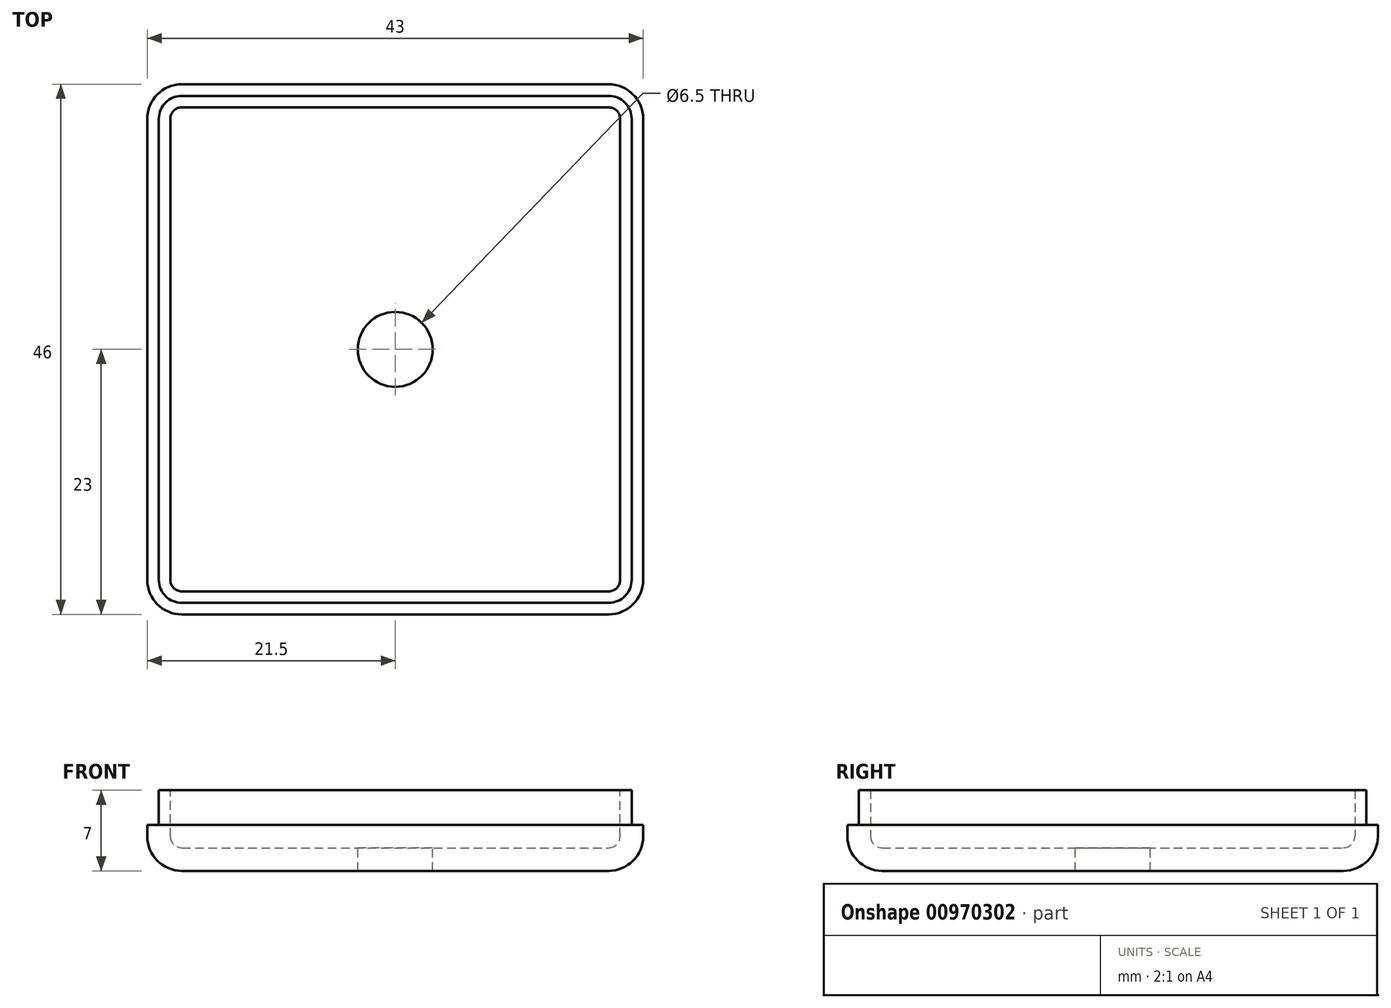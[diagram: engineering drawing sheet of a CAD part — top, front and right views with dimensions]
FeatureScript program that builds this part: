
annotation { "Feature Type Name" : "Feature", "Feature Type Description" : "" }
export const myFeature = defineFeature(function(context is Context, id is Id, definition is map)
    precondition{}
    {
        {
            var Q0;
            Q0=qCreatedBy(makeId("Top.planeOp"),FACE);
            var sketch = newSketch(context, id + "F0", { "sketchPlane" : qUnion([Q0])});
            skLineSegment(sketch, "E0.bottom", {"start": v(21.5, -23) * mm, "end": v(-21.5, -23) * mm});
            skLineSegment(sketch, "E0.top", {"start": v(21.5, 23) * mm, "end": v(-21.5, 23) * mm});
            skLineSegment(sketch, "E0.left", {"start": v(21.5, -23) * mm, "end": v(21.5, 23) * mm});
            skLineSegment(sketch, "E0.right", {"start": v(-21.5, -23) * mm, "end": v(-21.5, 23) * mm});
            skPoint(sketch, "E0.middle", {"position": v(0, 0) * mm});
            skSolve(sketch);
        }
        {
            var Q0;
            Q0=makeQuery(id+"F0.imprint","IMPRINT",FACE,{"disambiguationData":[TD([[makeQuery(id+"F0.imprint","IMPRINT",EDGE,{"derivedFrom":sQuery(id+"F0.wireOp",EDGE,"E0.bottom")}),-1.0]])]});
            extrude(context, id + "F1", {"entities" : qUnion([Q0]), "depth" : 7 * mm, "offsetDistance" : 25 * mm});
        }
        {
            var Q0;
            Q0=makeQuery(id+"F1.opExtrude","CAP_FACE",FACE,{"disambiguationData":[OSD([sQuery(id+"F0.wireOp",EDGE,"E0.bottom"),sQuery(id+"F0.wireOp",EDGE,"E0.top"),sQuery(id+"F0.wireOp",EDGE,"E0.left"),sQuery(id+"F0.wireOp",EDGE,"E0.right")])],"isStart":true});
            var Q1;
            Q1=makeQuery(id+"F1.opExtrude","SWEPT_EDGE",EDGE,{"disambiguationData":[OSD([sQuery(id+"F0.wireOp",EDGE,"E0.top"),sQuery(id+"F0.wireOp",EDGE,"E0.left")])]});
            var Q2;
            Q2=makeQuery(id+"F1.opExtrude","SWEPT_EDGE",EDGE,{"disambiguationData":[OSD([sQuery(id+"F0.wireOp",EDGE,"E0.bottom"),sQuery(id+"F0.wireOp",EDGE,"E0.left")])]});
            var Q3;
            Q3=makeQuery(id+"F1.opExtrude","SWEPT_EDGE",EDGE,{"disambiguationData":[OSD([sQuery(id+"F0.wireOp",EDGE,"E0.top"),sQuery(id+"F0.wireOp",EDGE,"E0.right")])]});
            var Q4;
            Q4=makeQuery(id+"F1.opExtrude","SWEPT_EDGE",EDGE,{"disambiguationData":[OSD([sQuery(id+"F0.wireOp",EDGE,"E0.bottom"),sQuery(id+"F0.wireOp",EDGE,"E0.right")])]});
            fillet(context, id + "F2", {"entities" : qUnion([Q0, Q1, Q2, Q3, Q4]), "radius" : 3 * mm, "tangentPropagation" : true, "allowEdgeOverflow" : false});
        }
        {
            var Q0;
            Q0=makeQuery(id+"F1.opExtrude","CAP_FACE",FACE,{"disambiguationData":[OSD([sQuery(id+"F0.wireOp",EDGE,"E0.bottom"),sQuery(id+"F0.wireOp",EDGE,"E0.top"),sQuery(id+"F0.wireOp",EDGE,"E0.left"),sQuery(id+"F0.wireOp",EDGE,"E0.right")])],"isStart":false});
            shell(context, id + "F3", {"entities" : qUnion([Q0]), "thickness" : 2 * mm});
        }
        {
            var Q0;
            Q0=makeQuery(id+"F3.opShell","OFFSET_FACE",FACE,{"disambiguationData":[OSD([sQuery(id+"F0.wireOp",EDGE,"E0.bottom"),sQuery(id+"F0.wireOp",EDGE,"E0.top"),sQuery(id+"F0.wireOp",EDGE,"E0.left"),sQuery(id+"F0.wireOp",EDGE,"E0.right")])]});
            var sketch = newSketch(context, id + "F4", { "sketchPlane" : qUnion([Q0])});
            skCircle(sketch, "E1", {"center": v(0, 0) * mm, "radius": 3.25 * mm});
            skSolve(sketch);
        }
        {
            var Q0;
            Q0=qSketchRegion(id+"F4",true);
            extrude(context, id + "F5", {"entities" : qUnion([Q0]), "operationType" : NewBodyOperationType.REMOVE, "endBound" : BoundingType.UP_TO_NEXT, "oppositeDirection" : true, "depth" : 25 * mm, "offsetDistance" : 25 * mm});
        }
        {
            var Q0;
            Q0=makeQuery(id+"F1.opExtrude","CAP_FACE",FACE,{"disambiguationData":[OSD([sQuery(id+"F0.wireOp",EDGE,"E0.bottom"),sQuery(id+"F0.wireOp",EDGE,"E0.top"),sQuery(id+"F0.wireOp",EDGE,"E0.left"),sQuery(id+"F0.wireOp",EDGE,"E0.right")])],"isStart":false});
            var sketch = newSketch(context, id + "F6", { "sketchPlane" : qUnion([Q0])});
            skArc(sketch, "E2.0", {"start": v(20.5, 20) * mm, "mid": v(19.91, 21.41) * mm, "end": v(18.5, 22) * mm});
            skLineSegment(sketch, "E2.1", {"start": v(20.5, -20) * mm, "end": v(20.5, 20) * mm});
            skLineSegment(sketch, "E2.2", {"start": v(18.5, 22) * mm, "end": v(-18.5, 22) * mm});
            skArc(sketch, "E2.3", {"start": v(18.5, -22) * mm, "mid": v(19.91, -21.41) * mm, "end": v(20.5, -20) * mm});
            skArc(sketch, "E2.4", {"start": v(-18.5, 22) * mm, "mid": v(-19.91, 21.41) * mm, "end": v(-20.5, 20) * mm});
            skLineSegment(sketch, "E2.5", {"start": v(-20.5, -20) * mm, "end": v(-20.5, 20) * mm});
            skArc(sketch, "E2.6", {"start": v(-20.5, -20) * mm, "mid": v(-19.91, -21.41) * mm, "end": v(-18.5, -22) * mm});
            skLineSegment(sketch, "E2.7", {"start": v(18.5, -22) * mm, "end": v(-18.5, -22) * mm});
            skLineSegment(sketch, "E3.bottom", {"start": v(25.92, -25.04) * mm, "end": v(-25.92, -25.04) * mm});
            skLineSegment(sketch, "E3.top", {"start": v(25.92, 25.04) * mm, "end": v(-25.92, 25.04) * mm});
            skLineSegment(sketch, "E3.left", {"start": v(25.92, -25.04) * mm, "end": v(25.92, 25.04) * mm});
            skLineSegment(sketch, "E3.right", {"start": v(-25.92, -25.04) * mm, "end": v(-25.92, 25.04) * mm});
            skPoint(sketch, "E3.middle", {"position": v(0, 0) * mm});
            skSolve(sketch);
        }
        {
            var Q0;
            Q0=qSketchRegion(id+"F6",true);
            extrude(context, id + "F7", {"entities" : qUnion([Q0]), "operationType" : NewBodyOperationType.REMOVE, "oppositeDirection" : true, "depth" : 3 * mm, "offsetDistance" : 25 * mm});
        }
    });
